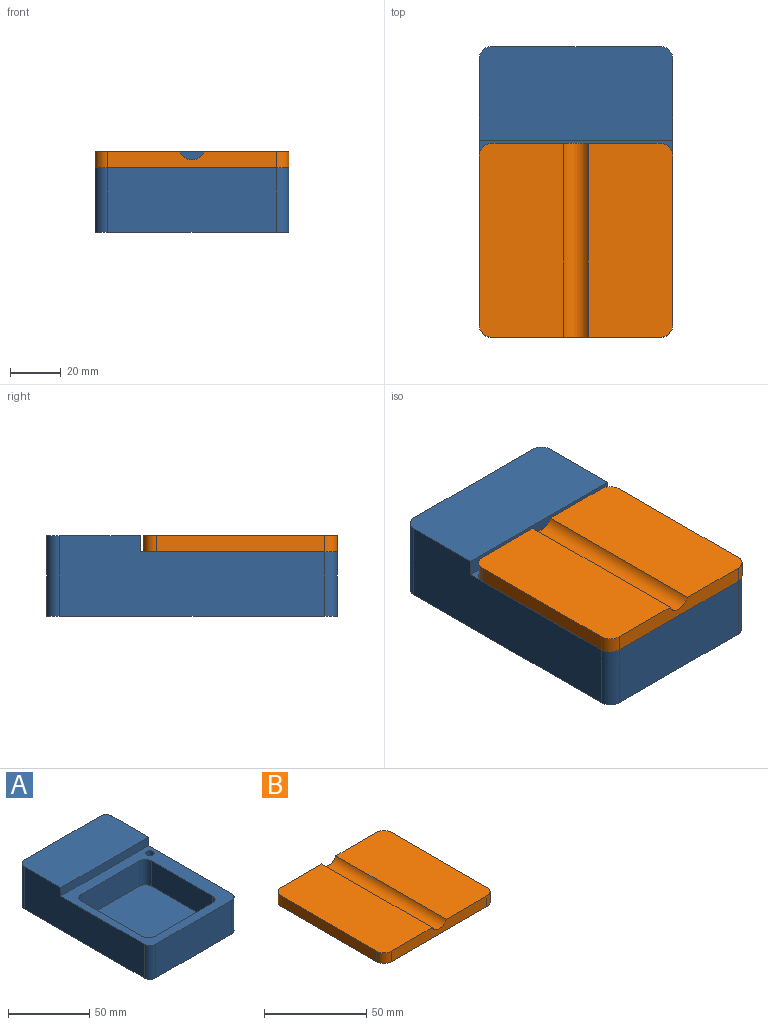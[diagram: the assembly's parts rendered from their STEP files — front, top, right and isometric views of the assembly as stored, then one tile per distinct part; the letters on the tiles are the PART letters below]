
ASSEMBLY  parts=2 mates=1
PART A: 22 faces, bbox 76.2x114.3x31.8 mm
  f0: plane 104.14x31.75mm, normal (1,0,0), area 2846.8mm2, adj f5,f6,f7,f10,f11,f12
  f1: plane 66.04x31.75mm, normal (0,1,0), area 2096.8mm2, adj f6,f7,f8,f12
  f2: plane 104.14x31.75mm, normal (-1,0,0), area 2846.8mm2, adj f5,f6,f8,f9,f11,f12
  f3: cylinder r=2.54mm len=25.4mm, axis (0,0,-1), area 405.4mm2, adj f5,f6
  f4: plane 66.04x25.4mm, normal (0,-1,0), area 1677.4mm2, adj f5,f6,f9,f10
  f5: plane 77.47x76.2mm, normal (0,0,1), area 2023.1mm2, adj f0,f2,f3,f4,f9,f10,f11,f13
  f6: plane 114.3x76.2mm, normal (0,0,-1), area 8667.2mm2, adj f0,f1,f2,f3,f4,f7,f8,f9
  f7: cylinder r=5.08mm len=31.75mm, axis (0,0,-1), area 253.4mm2, adj f0,f1,f6,f12
  f8: cylinder r=5.08mm len=31.75mm, axis (0,0,1), area 253.4mm2, adj f1,f2,f6,f12
  f9: cylinder r=5.08mm len=25.4mm, axis (0,0,-1), area 202.7mm2, adj f2,f4,f5,f6
  f10: cylinder r=5.08mm len=25.4mm, axis (0,0,1), area 202.7mm2, adj f0,f4,f5,f6
  f11: plane 76.2x6.35mm, normal (0,-1,0), area 483.9mm2, adj f0,f2,f5,f12
  f12: plane 76.2x36.83mm, normal (0,0,1), area 2795.4mm2, adj f0,f1,f2,f7,f8,f11
  f13: plane 53.34x19.05mm, normal (1,0,0), area 1016.1mm2, adj f5,f17,f18,f21
  f14: plane 50.8x19.05mm, normal (0,1,0), area 967.7mm2, adj f5,f17,f18,f19
  f15: plane 53.34x19.05mm, normal (-1,0,0), area 1016.1mm2, adj f5,f17,f19,f20
  f16: plane 50.8x19.05mm, normal (0,-1,0), area 967.7mm2, adj f5,f17,f20,f21
  f17: plane 63.5x60.96mm, normal (0,0,1), area 3848.8mm2, adj f13,f14,f15,f16,f18,f19,f20,f21
  f18: cylinder r=5.08mm len=19.05mm, axis (0,0,-1), area 152mm2, adj f5,f13,f14,f17
  f19: cylinder r=5.08mm len=19.05mm, axis (0,0,1), area 152mm2, adj f5,f14,f15,f17
  f20: cylinder r=5.08mm len=19.05mm, axis (0,0,-1), area 152mm2, adj f5,f15,f16,f17
  f21: cylinder r=5.08mm len=19.05mm, axis (0,0,1), area 152mm2, adj f5,f13,f16,f17
PART B: 14 faces, bbox 76.2x76.2x31.8 mm
  f0: plane 76.2x33.22mm, normal (0,0,1), area 2520.7mm2, adj f1,f2,f4,f7,f10,f11
  f1: plane 66.04x6.35mm, normal (1,0,0), area 419.4mm2, adj f0,f6,f7,f10
  f2: plane 66.04x6.35mm, normal (0,1,0), area 397.1mm2, adj f0,f5,f6,f7,f8,f11
  f3: plane 66.04x6.35mm, normal (-1,0,0), area 419.4mm2, adj f5,f6,f8,f9
  f4: plane 66.04x6.35mm, normal (0,-1,0), area 397.1mm2, adj f0,f5,f6,f9,f10,f11
  f5: plane 76.2x33.23mm, normal (0,0,1), area 2521.1mm2, adj f2,f3,f4,f8,f9,f11
  f6: plane 76.2x76.2mm, normal (0,0,-1), area 5764mm2, adj f1,f2,f3,f4,f7,f8,f9,f10
  f7: cylinder r=5.08mm len=6.35mm, axis (0,0,-1), area 50.7mm2, adj f0,f1,f2,f6
  f8: cylinder r=5.08mm len=6.35mm, axis (0,0,1), area 50.7mm2, adj f2,f3,f5,f6
  f9: cylinder r=5.08mm len=6.35mm, axis (0,0,-1), area 50.7mm2, adj f3,f4,f5,f6
  f10: cylinder r=5.08mm len=6.35mm, axis (0,0,1), area 50.7mm2, adj f0,f1,f4,f6
  f11: cylinder r=5.33mm len=76.2mm, axis (0,-1,0), area 937.6mm2, adj f0,f2,f4,f5
  f12: cylinder r=2.54mm len=25.4mm, axis (0,0,1), area 405.4mm2, adj f6,f13
  f13: plane 5.08x5.08mm, normal (0,0,-1), area 20.3mm2, adj f12
PLACE A t=(-9.29,-4.76,-2.27)mm fixed
PLACE B t=(-9.29,-23.81,13.6)mm
MATE revolute B.f7 <-> A.f3  axis (0,0,-1) through (23.73,9.21,-14.97)mm
